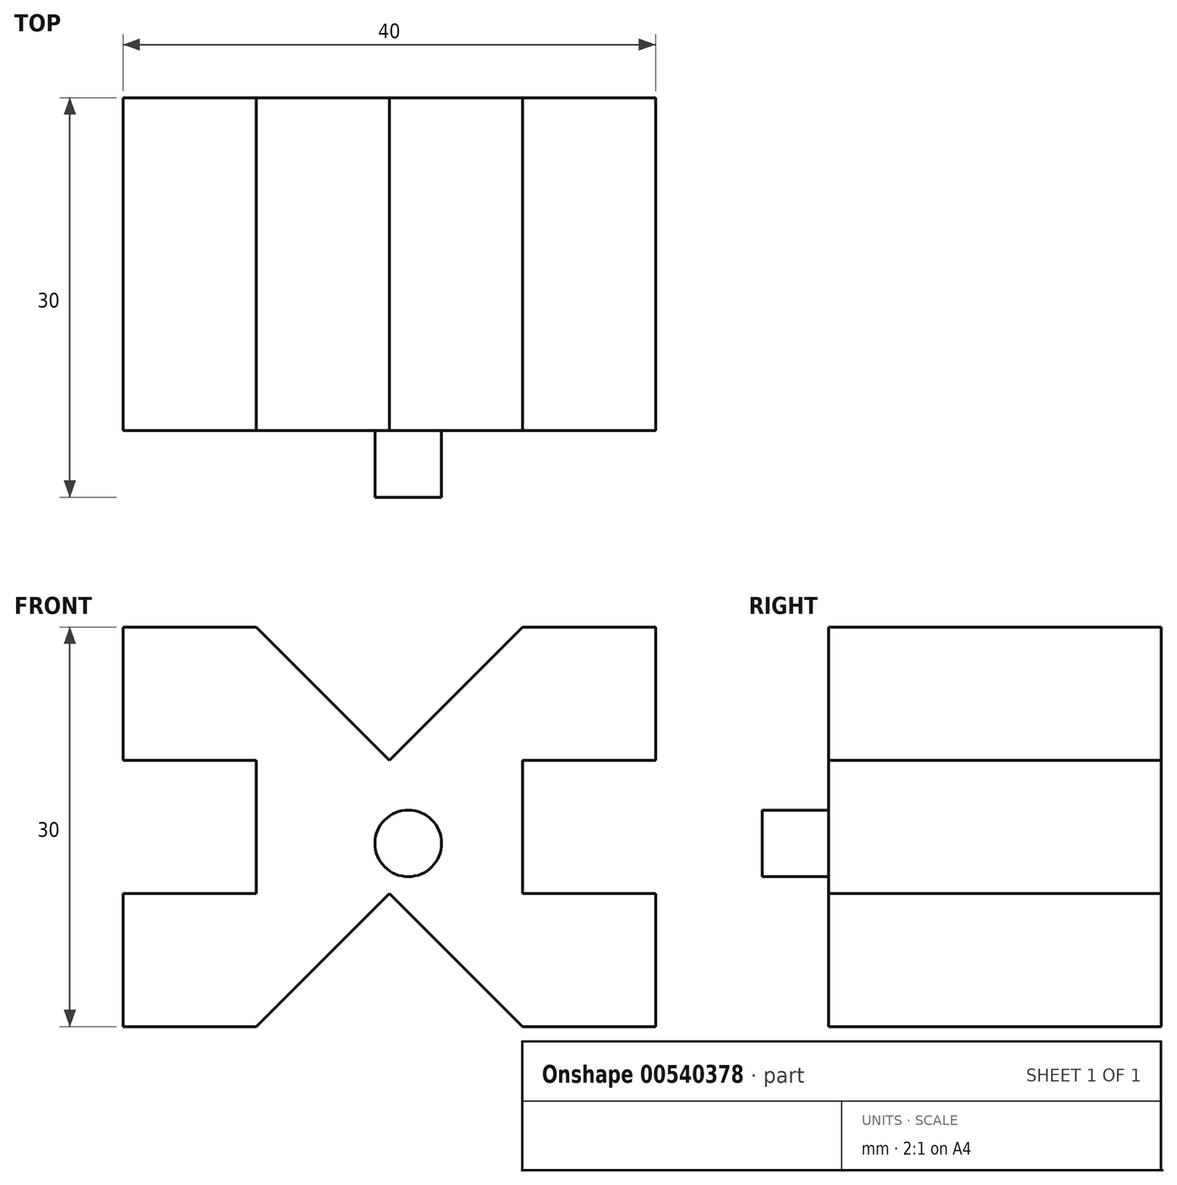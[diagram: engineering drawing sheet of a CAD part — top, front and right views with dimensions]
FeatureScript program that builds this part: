
annotation { "Feature Type Name" : "Feature", "Feature Type Description" : "" }
export const myFeature = defineFeature(function(context is Context, id is Id, definition is map)
    precondition{}
    {
        {
            var Q0;
            Q0=qCreatedBy(makeId("Front.planeOp"),FACE);
            var sketch = newSketch(context, id + "F0", { "sketchPlane" : qUnion([Q0])});
            skLineSegment(sketch, "E0", {"start": v(-10, 0) * mm, "end": v(-10, 5) * mm});
            skLineSegment(sketch, "E1", {"start": v(-10, 5) * mm, "end": v(-20, 5) * mm});
            skLineSegment(sketch, "E2", {"start": v(-20, 5) * mm, "end": v(-20, 15) * mm});
            skLineSegment(sketch, "E3", {"start": v(-20, 15) * mm, "end": v(-10, 15) * mm});
            skLineSegment(sketch, "E4", {"start": v(-10, 15) * mm, "end": v(0, 5) * mm});
            skLineSegment(sketch, "E5.MirrorCS", {"start": v(10, 15) * mm, "end": v(0, 5) * mm});
            skLineSegment(sketch, "E6.MirrorCS", {"start": v(20, 15) * mm, "end": v(10, 15) * mm});
            skLineSegment(sketch, "E7.MirrorCS", {"start": v(10, 0) * mm, "end": v(10, 5) * mm});
            skLineSegment(sketch, "E8.MirrorCS", {"start": v(20, 5) * mm, "end": v(20, 15) * mm});
            skLineSegment(sketch, "E9.MirrorCS", {"start": v(10, 5) * mm, "end": v(20, 5) * mm});
            skLineSegment(sketch, "E10.MirrorCS", {"start": v(10, -5) * mm, "end": v(20, -5) * mm});
            skLineSegment(sketch, "E11.MirrorCS", {"start": v(20, -5) * mm, "end": v(20, -15) * mm});
            skLineSegment(sketch, "E12.MirrorCS", {"start": v(10, 0) * mm, "end": v(10, -5) * mm});
            skLineSegment(sketch, "E13.MirrorCS", {"start": v(-20, -15) * mm, "end": v(-10, -15) * mm});
            skLineSegment(sketch, "E14.MirrorCS", {"start": v(20, -15) * mm, "end": v(10, -15) * mm});
            skLineSegment(sketch, "E15.MirrorCS", {"start": v(10, -15) * mm, "end": v(0, -5) * mm});
            skLineSegment(sketch, "E16.MirrorCS", {"start": v(-20, -5) * mm, "end": v(-20, -15) * mm});
            skLineSegment(sketch, "E17.MirrorCS", {"start": v(-10, 0) * mm, "end": v(-10, -5) * mm});
            skLineSegment(sketch, "E18.MirrorCS", {"start": v(-10, -5) * mm, "end": v(-20, -5) * mm});
            skLineSegment(sketch, "E19.MirrorCS", {"start": v(-10, -15) * mm, "end": v(0, -5) * mm});
            skSolve(sketch);
        }
        {
            var Q0;
            Q0=makeQuery(id+"F0.imprint","IMPRINT",FACE,{"disambiguationData":[TD([[makeQuery(id+"F0.imprint","IMPRINT",EDGE,{"derivedFrom":sQuery(id+"F0.wireOp",EDGE,"E0")}),-1.0]])]});
            extrude(context, id + "F1", {"entities" : qUnion([Q0]), "depth" : 25 * mm, "offsetDistance" : 25 * mm});
        }
        {
            var Q0;
            Q0=makeQuery(id+"F1.opExtrude","CAP_FACE",FACE,{"disambiguationData":[OSD([sQuery(id+"F0.wireOp",EDGE,"E0"),sQuery(id+"F0.wireOp",EDGE,"E1"),sQuery(id+"F0.wireOp",EDGE,"E2"),sQuery(id+"F0.wireOp",EDGE,"E3"),sQuery(id+"F0.wireOp",EDGE,"E4"),sQuery(id+"F0.wireOp",EDGE,"E5.MirrorCS"),sQuery(id+"F0.wireOp",EDGE,"E6.MirrorCS"),sQuery(id+"F0.wireOp",EDGE,"E7.MirrorCS"),sQuery(id+"F0.wireOp",EDGE,"E8.MirrorCS"),sQuery(id+"F0.wireOp",EDGE,"E9.MirrorCS"),sQuery(id+"F0.wireOp",EDGE,"E10.MirrorCS"),sQuery(id+"F0.wireOp",EDGE,"E11.MirrorCS"),sQuery(id+"F0.wireOp",EDGE,"E12.MirrorCS"),sQuery(id+"F0.wireOp",EDGE,"E13.MirrorCS"),sQuery(id+"F0.wireOp",EDGE,"E14.MirrorCS"),sQuery(id+"F0.wireOp",EDGE,"E15.MirrorCS"),sQuery(id+"F0.wireOp",EDGE,"E16.MirrorCS"),sQuery(id+"F0.wireOp",EDGE,"E17.MirrorCS"),sQuery(id+"F0.wireOp",EDGE,"E18.MirrorCS"),sQuery(id+"F0.wireOp",EDGE,"E19.MirrorCS")])],"isStart":false});
            var sketch = newSketch(context, id + "F2", { "sketchPlane" : qUnion([Q0])});
            skSolve(sketch);
        }
        {
            var Q0;
            Q0=makeQuery(id+"F2.imprint","IMPRINT",FACE,{"disambiguationData":[TD([[makeQuery(id+"F2.imprint","IMPRINT",EDGE,{"derivedFrom":makeQuery(id+"F1.opExtrude","CAP_EDGE",EDGE,{"disambiguationData":[OSD([sQuery(id+"F0.wireOp",EDGE,"E1")])],"isStart":false})}),-1.0]])]});
            var sketch = newSketch(context, id + "F3", { "sketchPlane" : qUnion([Q0])});
            skCircle(sketch, "E20", {"center": v(1.42, -1.24) * mm, "radius": 2.5 * mm});
            skSolve(sketch);
        }
        {
            var Q0;
            Q0=makeQuery(id+"F3.imprint","IMPRINT",FACE,{"disambiguationData":[TD([[makeQuery(id+"F3.imprint","IMPRINT",EDGE,{"derivedFrom":sQuery(id+"F3.wireOp",EDGE,"E20")}),1.0]])]});
            extrude(context, id + "F4", {"entities" : qUnion([Q0]), "operationType" : NewBodyOperationType.ADD, "depth" : 5 * mm, "offsetDistance" : 25 * mm});
        }
    });
